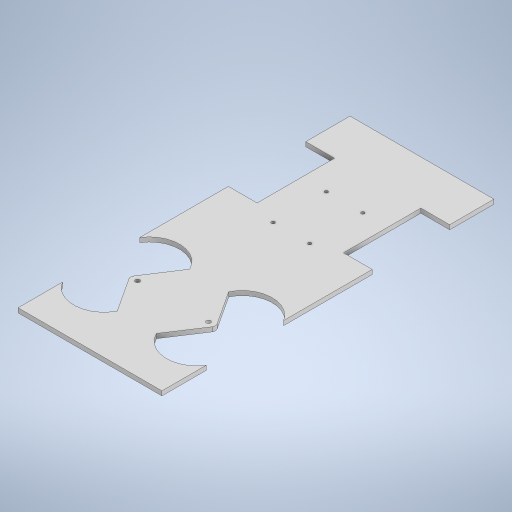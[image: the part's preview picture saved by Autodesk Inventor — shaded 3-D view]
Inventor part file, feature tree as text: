
AUTODESK INVENTOR PART (.ipt)
format: ipt  version: 2023.2 (Build 272271000, 271)  size: 338,944 bytes
history: native  units: mm
features: sketch x3, hole x2
ambient origin geometry x8: Origin, YZ Plane, XZ Plane, XY Plane, X Axis, Y Axis, Z Axis, Center Point
bodies: Body1 (feature_tree)
feature tree (5):
  hole  "Hole1"  [1 undecoded]
  hole  "Hole2"  [1 undecoded]
  sketch  "Sketch1"  dims[d122=130.0mm d123=300.0mm]
  sketch  "Sketch12"  dims[d159=6.108652mm d160=6.108652mm d161=4.0mm d169=6.108652mm d170=6.108652mm d172=75.0mm d175=33.0mm d179=33.0mm d181=4.0mm d182=0.0mm d183=70.0mm d185=26.0mm d186=35.0mm d187=26.0mm d188=75.0mm d189=70.0mm d190=26.0mm d191=75.0mm d196=3.0mm d201=33.0mm d202=48.0mm d205=75.0mm d208=3.0mm d209=5.0mm d210=3.0mm d211=6.0mm d212=4.0mm d213=2.0mm d214=90.0deg d215=8.0mm d216=20.594885mm d217=75.0mm d219=4.0mm d220=33.0mm d221=4.0mm d222=6.0mm d223=4.0mm d224=2.0mm d225=90.0deg d226=8.0mm d227=20.594885mm d9=0.5mm d10=0.872665mm d11=0.5mm d12=0.872665mm d13=0.5mm d14=0.872665mm d27=0.5mm d28=0.872665mm d29=0.5mm d30=0.872665mm d88=0.5mm d89=0.872665mm d90=0.5mm d91=0.872665mm d116=0.5mm d117=0.872665mm d118=0.5mm d119=0.872665mm d154=0.5mm d155=0.872665mm d156=0.5mm d157=0.872665mm d184=0.872665mm]
  sketch  "Sketch3"  dims[d128=75.0mm d158=33.0mm]
note: 2 required parameter values undecoded (feature->parameter linkage not recoverable at this tier; creation-order binding heuristic only, values carry confidence <= 0.55)
